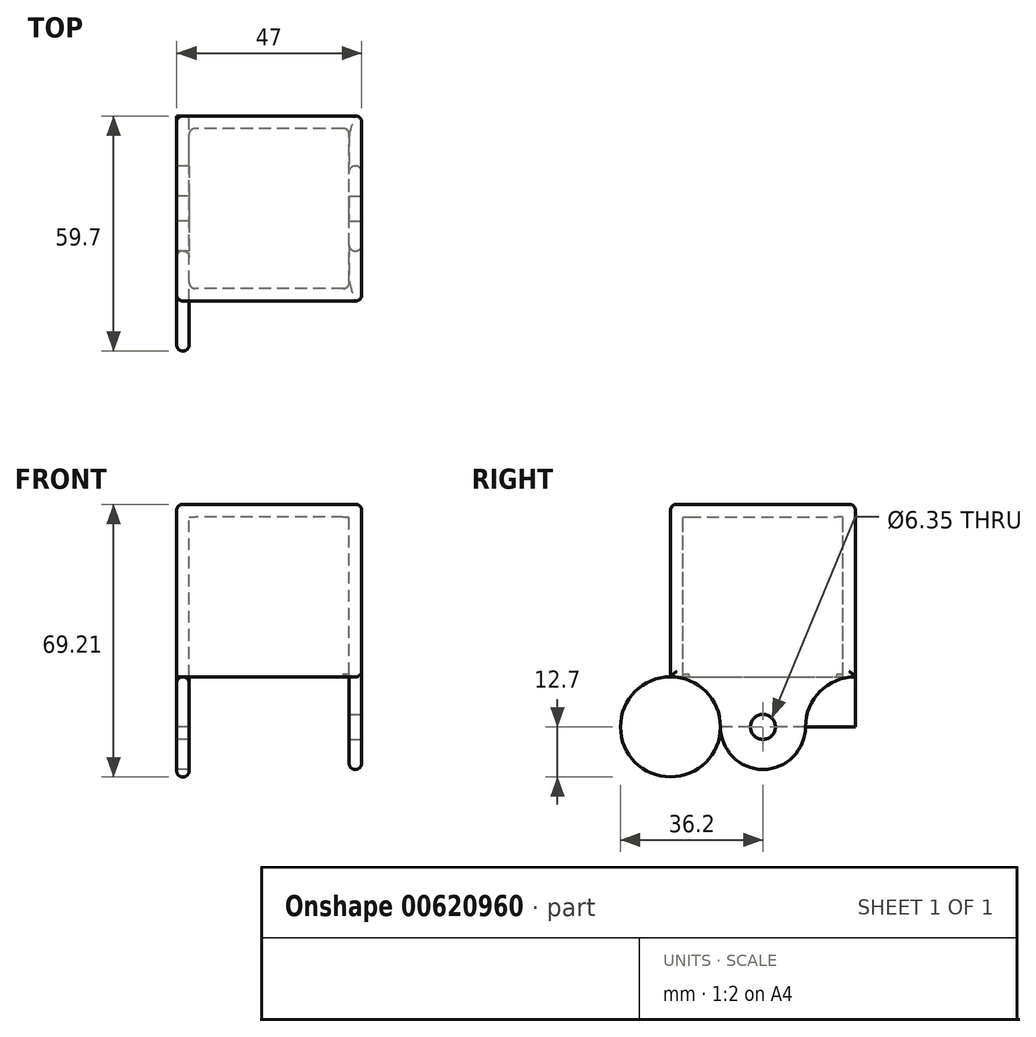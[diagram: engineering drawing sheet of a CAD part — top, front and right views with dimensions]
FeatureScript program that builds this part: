
annotation { "Feature Type Name" : "Feature", "Feature Type Description" : "" }
export const myFeature = defineFeature(function(context is Context, id is Id, definition is map)
    precondition{}
    {
        {
            var Q0;
            Q0=qCreatedBy(makeId("Top.planeOp"),FACE);
            var sketch = newSketch(context, id + "F0", { "sketchPlane" : qUnion([Q0])});
            skLineSegment(sketch, "E0.bottom", {"start": v(20.32, -20.32) * mm, "end": v(-20.32, -20.32) * mm});
            skLineSegment(sketch, "E0.top", {"start": v(20.32, 20.32) * mm, "end": v(-20.32, 20.32) * mm});
            skLineSegment(sketch, "E0.left", {"start": v(20.32, -20.32) * mm, "end": v(20.32, 20.32) * mm});
            skLineSegment(sketch, "E0.right", {"start": v(-20.32, -20.32) * mm, "end": v(-20.32, 20.32) * mm});
            skPoint(sketch, "E0.middle", {"position": v(0, 0) * mm});
            skLineSegment(sketch, "E1.0", {"start": v(-23.5, -20.32) * mm, "end": v(-23.5, 20.32) * mm});
            skLineSegment(sketch, "E1.1", {"start": v(20.32, -23.5) * mm, "end": v(-20.32, -23.5) * mm});
            skLineSegment(sketch, "E1.2", {"start": v(23.5, -20.32) * mm, "end": v(23.5, 20.32) * mm});
            skLineSegment(sketch, "E1.3", {"start": v(20.32, 23.5) * mm, "end": v(-20.32, 23.5) * mm});
            skPoint(sketch, "E2.visualSharp", {"position": v(-23.5, 23.5) * mm});
            skPoint(sketch, "E3.visualSharp", {"position": v(23.5, 23.5) * mm});
            skPoint(sketch, "E4.visualSharp", {"position": v(23.5, -23.5) * mm});
            skPoint(sketch, "E5.visualSharp", {"position": v(-23.5, -23.5) * mm});
            skLineSegment(sketch, "E6.bottom", {"start": v(20.32, 20.32) * mm, "end": v(23.5, 20.32) * mm});
            skLineSegment(sketch, "E6.top", {"start": v(20.32, 23.5) * mm, "end": v(23.5, 23.5) * mm});
            skLineSegment(sketch, "E6.left", {"start": v(20.32, 20.32) * mm, "end": v(20.32, 23.5) * mm});
            skLineSegment(sketch, "E6.right", {"start": v(23.5, 20.32) * mm, "end": v(23.5, 23.5) * mm});
            skLineSegment(sketch, "E7.bottom", {"start": v(20.32, -20.32) * mm, "end": v(23.5, -20.32) * mm});
            skLineSegment(sketch, "E7.top", {"start": v(20.32, -23.5) * mm, "end": v(23.5, -23.5) * mm});
            skLineSegment(sketch, "E7.left", {"start": v(20.32, -20.32) * mm, "end": v(20.32, -23.5) * mm});
            skLineSegment(sketch, "E7.right", {"start": v(23.5, -20.32) * mm, "end": v(23.5, -23.5) * mm});
            skLineSegment(sketch, "E8.bottom", {"start": v(-23.5, -23.5) * mm, "end": v(-20.32, -23.5) * mm});
            skLineSegment(sketch, "E8.top", {"start": v(-23.5, -20.32) * mm, "end": v(-20.32, -20.32) * mm});
            skLineSegment(sketch, "E8.left", {"start": v(-23.5, -23.5) * mm, "end": v(-23.5, -20.32) * mm});
            skLineSegment(sketch, "E8.right", {"start": v(-20.32, -23.5) * mm, "end": v(-20.32, -20.32) * mm});
            skLineSegment(sketch, "E9.bottom", {"start": v(-23.5, 23.5) * mm, "end": v(-20.32, 23.5) * mm});
            skLineSegment(sketch, "E9.top", {"start": v(-23.5, 20.32) * mm, "end": v(-20.32, 20.32) * mm});
            skLineSegment(sketch, "E9.left", {"start": v(-23.5, 23.5) * mm, "end": v(-23.5, 20.32) * mm});
            skLineSegment(sketch, "E9.right", {"start": v(-20.32, 23.5) * mm, "end": v(-20.32, 20.32) * mm});
            skSolve(sketch);
        }
        {
            var Q0;
            Q0=makeQuery(id+"F0.imprint","IMPRINT",FACE,{"disambiguationData":[TD([[makeQuery(id+"F0.imprint","IMPRINT",EDGE,{"derivedFrom":sQuery(id+"F0.wireOp",EDGE,"E0.bottom")}),-1.0]])]});
            var Q1;
            Q1=makeQuery(id+"F0.imprint","IMPRINT",FACE,{"disambiguationData":[TD([[makeQuery(id+"F0.imprint","IMPRINT",EDGE,{"derivedFrom":sQuery(id+"F0.wireOp",EDGE,"E0.bottom")}),1.0]])]});
            var Q2;
            Q2=makeQuery(id+"F0.imprint","IMPRINT",FACE,{"disambiguationData":[TD([[makeQuery(id+"F0.imprint","IMPRINT",EDGE,{"derivedFrom":sQuery(id+"F0.wireOp",EDGE,"E7.bottom")}),-1.0]])]});
            var Q3;
            Q3=makeQuery(id+"F0.imprint","IMPRINT",FACE,{"disambiguationData":[TD([[makeQuery(id+"F0.imprint","IMPRINT",EDGE,{"derivedFrom":sQuery(id+"F0.wireOp",EDGE,"E6.bottom")}),1.0]])]});
            var Q4;
            Q4=makeQuery(id+"F0.imprint","IMPRINT",FACE,{"disambiguationData":[TD([[makeQuery(id+"F0.imprint","IMPRINT",EDGE,{"derivedFrom":sQuery(id+"F0.wireOp",EDGE,"E0.top")}),-1.0]])]});
            var Q5;
            Q5=makeQuery(id+"F0.imprint","IMPRINT",FACE,{"disambiguationData":[TD([[makeQuery(id+"F0.imprint","IMPRINT",EDGE,{"derivedFrom":sQuery(id+"F0.wireOp",EDGE,"E9.bottom")}),-1.0]])]});
            var Q6;
            Q6=makeQuery(id+"F0.imprint","IMPRINT",FACE,{"disambiguationData":[TD([[makeQuery(id+"F0.imprint","IMPRINT",EDGE,{"derivedFrom":sQuery(id+"F0.wireOp",EDGE,"E0.right")}),1.0]])]});
            var Q7;
            Q7=makeQuery(id+"F0.imprint","IMPRINT",FACE,{"disambiguationData":[TD([[makeQuery(id+"F0.imprint","IMPRINT",EDGE,{"derivedFrom":sQuery(id+"F0.wireOp",EDGE,"E8.bottom")}),1.0]])]});
            var Q8;
            Q8=makeQuery(id+"F0.imprint","IMPRINT",FACE,{"disambiguationData":[TD([[makeQuery(id+"F0.imprint","IMPRINT",EDGE,{"derivedFrom":sQuery(id+"F0.wireOp",EDGE,"E0.left")}),-1.0]])]});
            extrude(context, id + "F1", {"entities" : qUnion([Q0, Q1, Q2, Q3, Q4, Q5, Q6, Q7, Q8]), "depth" : 3.17 * mm, "offsetDistance" : 25.4 * mm});
        }
        {
            var Q0;
            Q0=makeQuery(id+"F0.imprint","IMPRINT",FACE,{"disambiguationData":[TD([[makeQuery(id+"F0.imprint","IMPRINT",EDGE,{"derivedFrom":sQuery(id+"F0.wireOp",EDGE,"E0.bottom")}),1.0]])]});
            var Q1;
            Q1=makeQuery(id+"F0.imprint","IMPRINT",FACE,{"disambiguationData":[TD([[makeQuery(id+"F0.imprint","IMPRINT",EDGE,{"derivedFrom":sQuery(id+"F0.wireOp",EDGE,"E8.bottom")}),1.0]])]});
            var Q2;
            Q2=makeQuery(id+"F0.imprint","IMPRINT",FACE,{"disambiguationData":[TD([[makeQuery(id+"F0.imprint","IMPRINT",EDGE,{"derivedFrom":sQuery(id+"F0.wireOp",EDGE,"E0.right")}),1.0]])]});
            var Q3;
            Q3=makeQuery(id+"F0.imprint","IMPRINT",FACE,{"disambiguationData":[TD([[makeQuery(id+"F0.imprint","IMPRINT",EDGE,{"derivedFrom":sQuery(id+"F0.wireOp",EDGE,"E9.bottom")}),-1.0]])]});
            var Q4;
            Q4=makeQuery(id+"F0.imprint","IMPRINT",FACE,{"disambiguationData":[TD([[makeQuery(id+"F0.imprint","IMPRINT",EDGE,{"derivedFrom":sQuery(id+"F0.wireOp",EDGE,"E0.top")}),-1.0]])]});
            var Q5;
            Q5=makeQuery(id+"F0.imprint","IMPRINT",FACE,{"disambiguationData":[TD([[makeQuery(id+"F0.imprint","IMPRINT",EDGE,{"derivedFrom":sQuery(id+"F0.wireOp",EDGE,"E6.bottom")}),1.0]])]});
            var Q6;
            Q6=makeQuery(id+"F0.imprint","IMPRINT",FACE,{"disambiguationData":[TD([[makeQuery(id+"F0.imprint","IMPRINT",EDGE,{"derivedFrom":sQuery(id+"F0.wireOp",EDGE,"E0.left")}),-1.0]])]});
            var Q7;
            Q7=makeQuery(id+"F0.imprint","IMPRINT",FACE,{"disambiguationData":[TD([[makeQuery(id+"F0.imprint","IMPRINT",EDGE,{"derivedFrom":sQuery(id+"F0.wireOp",EDGE,"E7.bottom")}),-1.0]])]});
            extrude(context, id + "F2", {"entities" : qUnion([Q0, Q1, Q2, Q3, Q4, Q5, Q6, Q7]), "operationType" : NewBodyOperationType.ADD, "oppositeDirection" : true, "depth" : 40.64 * mm, "offsetDistance" : 25.4 * mm});
        }
        {
            var Q0;
            {var subQ0=sQuery(id+"F0.wireOp",EDGE,"E1.2");Q0=makeQuery(id+"F2.boolean.opBoolean","MERGE",FACE,{"derivedFrom":[makeQuery(id+"F1.opExtrude","SWEPT_FACE",FACE,{"disambiguationData":[OSD([subQ0])]}),makeQuery(id+"F2.opExtrude","SWEPT_FACE",FACE,{"disambiguationData":[OSD([subQ0])]})]});}
            var sketch = newSketch(context, id + "F3", { "sketchPlane" : qUnion([Q0])});
            skLineSegment(sketch, "E10", {"start": v(23.5, -40.64) * mm, "end": v(23.5, -53.34) * mm});
            skCircle(sketch, "E11", {"center": v(23.5, -53.34) * mm, "radius": 12.7 * mm});
            skLineSegment(sketch, "E12", {"start": v(23.5, -53.34) * mm, "end": v(-23.5, -53.34) * mm});
            skCircle(sketch, "E13", {"center": v(0, -53.34) * mm, "radius": 10.8 * mm});
            skCircle(sketch, "E14", {"center": v(-23.5, -53.34) * mm, "radius": 12.7 * mm});
            skCircle(sketch, "E15", {"center": v(0, -53.34) * mm, "radius": 3.18 * mm});
            skSolve(sketch);
        }
        {
            var Q0;
            {var subQ0=sQuery(id+"F3.wireOp",EDGE,"E11");var subQ5=sQuery(id+"F3.wireOp",EDGE,"E13");var subQ6=makeQuery(id+"F3.imprint","INTERSECT",VERTEX,{"derivedFrom":[subQ0,sQuery(id+"F3.wireOp",EDGE,"E12"),subQ5]});Q0=makeQuery(id+"F3.imprint","IMPRINT",FACE,{"disambiguationData":[TD([[makeQuery(id+"F3.imprint","IMPRINT",EDGE,{"disambiguationData":[TD([[subQ6,-1.0]])],"derivedFrom":subQ5}),-1.0]])]});}
            var Q1;
            {var subQ1=sQuery(id+"F3.wireOp",EDGE,"E12");var subQ5=sQuery(id+"F3.wireOp",EDGE,"E15");var subQ7=makeQuery(id+"F3.imprint","INTERSECT",VERTEX,{"disambiguationData":[OD(0.0)],"derivedFrom":[subQ1,subQ5]});Q1=makeQuery(id+"F3.imprint","IMPRINT",FACE,{"disambiguationData":[TD([[makeQuery(id+"F3.imprint","IMPRINT",EDGE,{"disambiguationData":[TD([[subQ7,-1.0]])],"derivedFrom":subQ5}),-1.0]])]});}
            var Q2;
            {var subQ0=sQuery(id+"F3.wireOp",EDGE,"E15");var subQ1=sQuery(id+"F3.wireOp",EDGE,"E12");var subQ2=makeQuery(id+"F3.imprint","INTERSECT",VERTEX,{"disambiguationData":[OD(0.0)],"derivedFrom":[subQ1,subQ0]});Q2=makeQuery(id+"F3.imprint","IMPRINT",FACE,{"disambiguationData":[TD([[makeQuery(id+"F3.imprint","IMPRINT",EDGE,{"disambiguationData":[TD([[subQ2,1.0]])],"derivedFrom":subQ0}),-1.0]])]});}
            var Q3;
            {var subQ0=sQuery(id+"F3.wireOp",EDGE,"E14");var subQ1=sQuery(id+"F3.wireOp",EDGE,"E13");var subQ2=makeQuery(id+"F3.imprint","INTERSECT",VERTEX,{"derivedFrom":[sQuery(id+"F3.wireOp",EDGE,"E12"),subQ1,subQ0]});Q3=makeQuery(id+"F3.imprint","IMPRINT",FACE,{"disambiguationData":[TD([[makeQuery(id+"F3.imprint","IMPRINT",EDGE,{"disambiguationData":[TD([[subQ2,1.0]])],"derivedFrom":subQ1}),-1.0]])]});}
            extrude(context, id + "F4", {"entities" : qUnion([Q0, Q1, Q2, Q3]), "operationType" : NewBodyOperationType.ADD, "oppositeDirection" : true, "depth" : 3.17 * mm, "offsetDistance" : 25.4 * mm});
        }
        {
            var Q0;
            {var subQ0=sQuery(id+"F0.wireOp",EDGE,"E9.left");var subQ1=sQuery(id+"F0.wireOp",EDGE,"E8.left");var subQ2=sQuery(id+"F0.wireOp",EDGE,"E1.0");Q0=makeQuery(id+"F2.boolean.opBoolean","MERGE",FACE,{"derivedFrom":[makeQuery(id+"F1.opExtrude","SWEPT_FACE",FACE,{"disambiguationData":[OSD([subQ2,subQ1,subQ0])]}),makeQuery(id+"F2.opExtrude","SWEPT_FACE",FACE,{"disambiguationData":[OSD([subQ2,subQ1,subQ0])]})]});}
            var sketch = newSketch(context, id + "F5", { "sketchPlane" : qUnion([Q0])});
            skArc(sketch, "E16.0.0", {"start": v(23.5, -40.64) * mm, "mid": v(32.48, -62.32) * mm, "end": v(10.8, -53.34) * mm});
            skArc(sketch, "E16.0.1", {"start": v(10.8, -53.34) * mm, "mid": v(14.51, -44.36) * mm, "end": v(23.5, -40.64) * mm});
            skLineSegment(sketch, "E17.0.0", {"start": v(-23.5, -53.34) * mm, "end": v(-23.5, -40.64) * mm});
            skArc(sketch, "E17.0.1", {"start": v(-23.5, -40.64) * mm, "mid": v(-14.51, -44.36) * mm, "end": v(-10.8, -53.34) * mm});
            skLineSegment(sketch, "E17.0.2", {"start": v(-10.8, -53.34) * mm, "end": v(-23.5, -53.34) * mm});
            skArc(sketch, "E18.0.0", {"start": v(-3.17, -53.34) * mm, "mid": v(0, -56.52) * mm, "end": v(3.18, -53.34) * mm});
            skLineSegment(sketch, "E18.0.1", {"start": v(3.18, -53.34) * mm, "end": v(10.8, -53.34) * mm});
            skArc(sketch, "E18.0.2", {"start": v(10.8, -53.34) * mm, "mid": v(0, -64.14) * mm, "end": v(-10.8, -53.34) * mm});
            skLineSegment(sketch, "E18.0.3", {"start": v(-10.8, -53.34) * mm, "end": v(-3.17, -53.34) * mm});
            skLineSegment(sketch, "E19.0.0", {"start": v(10.8, -53.34) * mm, "end": v(3.18, -53.34) * mm});
            skArc(sketch, "E19.0.1", {"start": v(3.18, -53.34) * mm, "mid": v(0, -50.17) * mm, "end": v(-3.17, -53.34) * mm});
            skLineSegment(sketch, "E19.0.2", {"start": v(-3.17, -53.34) * mm, "end": v(-10.8, -53.34) * mm});
            skArc(sketch, "E19.0.3", {"start": v(-10.8, -53.34) * mm, "mid": v(0, -42.55) * mm, "end": v(10.8, -53.34) * mm});
            skLineSegment(sketch, "E19.0.4", {"start": v(10.8, -53.34) * mm, "end": v(10.8, -53.34) * mm});
            skSolve(sketch);
        }
        {
            var Q0;
            {var subQ0=sQuery(id+"F5.wireOp",EDGE,"E16.0.1");Q0=makeQuery(id+"F5.imprint","IMPRINT",FACE,{"disambiguationData":[TD([[makeQuery(id+"F5.imprint","IMPRINT",EDGE,{"derivedFrom":subQ0}),1.0]])]});}
            var Q1;
            Q1=makeQuery(id+"F5.imprint","IMPRINT",FACE,{"disambiguationData":[TD([[makeQuery(id+"F5.imprint","IMPRINT",EDGE,{"derivedFrom":sQuery(id+"F5.wireOp",EDGE,"E19.0.0")}),-1.0]])]});
            var Q2;
            Q2=makeQuery(id+"F5.imprint","IMPRINT",FACE,{"disambiguationData":[TD([[makeQuery(id+"F5.imprint","IMPRINT",EDGE,{"derivedFrom":sQuery(id+"F5.wireOp",EDGE,"E18.0.0")}),-1.0]])]});
            var Q3;
            {var subQ0=sQuery(id+"F5.wireOp",EDGE,"E17.0.1");Q3=makeQuery(id+"F5.imprint","IMPRINT",FACE,{"disambiguationData":[TD([[makeQuery(id+"F5.imprint","IMPRINT",EDGE,{"derivedFrom":subQ0}),1.0]])]});}
            extrude(context, id + "F6", {"entities" : qUnion([Q0, Q1, Q2, Q3]), "operationType" : NewBodyOperationType.ADD, "oppositeDirection" : true, "depth" : 3.17 * mm, "offsetDistance" : 25.4 * mm});
        }
        {
            var Q0;
            {var subQ0=sQuery(id+"F0.wireOp",EDGE,"E6.right");var subQ1=sQuery(id+"F0.wireOp",EDGE,"E6.top");Q0=makeQuery(id+"F2.boolean.opBoolean","MERGE",EDGE,{"derivedFrom":[makeQuery(id+"F1.opExtrude","SWEPT_EDGE",EDGE,{"disambiguationData":[OSD([subQ1,subQ0])]}),makeQuery(id+"F2.opExtrude","SWEPT_EDGE",EDGE,{"disambiguationData":[OSD([subQ1,subQ0])]})]});}
            var Q1;
            {var subQ0=sQuery(id+"F0.wireOp",EDGE,"E9.left");var subQ1=sQuery(id+"F0.wireOp",EDGE,"E9.bottom");Q1=makeQuery(id+"F2.boolean.opBoolean","MERGE",EDGE,{"derivedFrom":[makeQuery(id+"F1.opExtrude","SWEPT_EDGE",EDGE,{"disambiguationData":[OSD([subQ1,subQ0])]}),makeQuery(id+"F2.opExtrude","SWEPT_EDGE",EDGE,{"disambiguationData":[OSD([subQ1,subQ0])]})]});}
            var Q2;
            Q2=makeQuery(id+"F1.opExtrude","CAP_EDGE",EDGE,{"disambiguationData":[OSD([sQuery(id+"F0.wireOp",EDGE,"E1.3"),sQuery(id+"F0.wireOp",EDGE,"E6.top"),sQuery(id+"F0.wireOp",EDGE,"E9.bottom")])],"isStart":false});
            var Q3;
            Q3=makeQuery(id+"F1.opExtrude","CAP_EDGE",EDGE,{"disambiguationData":[OSD([sQuery(id+"F0.wireOp",EDGE,"E1.2"),sQuery(id+"F0.wireOp",EDGE,"E6.right"),sQuery(id+"F0.wireOp",EDGE,"E7.right")])],"isStart":false});
            var Q4;
            Q4=makeQuery(id+"F1.opExtrude","CAP_EDGE",EDGE,{"disambiguationData":[OSD([sQuery(id+"F0.wireOp",EDGE,"E1.1"),sQuery(id+"F0.wireOp",EDGE,"E7.top"),sQuery(id+"F0.wireOp",EDGE,"E8.bottom")])],"isStart":false});
            var Q5;
            Q5=makeQuery(id+"F1.opExtrude","CAP_EDGE",EDGE,{"disambiguationData":[OSD([sQuery(id+"F0.wireOp",EDGE,"E1.0"),sQuery(id+"F0.wireOp",EDGE,"E8.left"),sQuery(id+"F0.wireOp",EDGE,"E9.left")])],"isStart":false});
            var Q6;
            {var subQ0=sQuery(id+"F0.wireOp",EDGE,"E7.right");var subQ1=sQuery(id+"F0.wireOp",EDGE,"E7.top");Q6=makeQuery(id+"F2.boolean.opBoolean","MERGE",EDGE,{"derivedFrom":[makeQuery(id+"F1.opExtrude","SWEPT_EDGE",EDGE,{"disambiguationData":[OSD([subQ1,subQ0])]}),makeQuery(id+"F2.opExtrude","SWEPT_EDGE",EDGE,{"disambiguationData":[OSD([subQ1,subQ0])]})]});}
            var Q7;
            {var subQ0=sQuery(id+"F0.wireOp",EDGE,"E8.left");var subQ1=sQuery(id+"F0.wireOp",EDGE,"E8.bottom");Q7=makeQuery(id+"F2.boolean.opBoolean","MERGE",EDGE,{"derivedFrom":[makeQuery(id+"F1.opExtrude","SWEPT_EDGE",EDGE,{"disambiguationData":[OSD([subQ1,subQ0])]}),makeQuery(id+"F2.opExtrude","SWEPT_EDGE",EDGE,{"disambiguationData":[OSD([subQ1,subQ0])]})]});}
            var Q8;
            Q8=makeQuery(id+"F6.opExtrude","CAP_EDGE",EDGE,{"disambiguationData":[OSD([sQuery(id+"F5.wireOp",EDGE,"E16.0.1")])],"isStart":true});
            var Q9;
            Q9=makeQuery(id+"F4.opExtrude","CAP_EDGE",EDGE,{"disambiguationData":[OSD([sQuery(id+"F3.wireOp",EDGE,"E14")])],"isStart":true});
            var Q10;
            Q10=makeQuery(id+"F4.opExtrude","CAP_EDGE",EDGE,{"disambiguationData":[OSD([sQuery(id+"F3.wireOp",EDGE,"E14")])],"isStart":false});
            var Q11;
            Q11=makeQuery(id+"F6.opExtrude","CAP_EDGE",EDGE,{"disambiguationData":[OSD([sQuery(id+"F5.wireOp",EDGE,"E16.0.1")])],"isStart":false});
            fillet(context, id + "F7", {"entities" : qUnion([Q0, Q1, Q2, Q3, Q4, Q5, Q6, Q7, Q8, Q9, Q10, Q11]), "radius" : 1.52 * mm, "tangentPropagation" : true, "allowEdgeOverflow" : false});
        }
        {
            var Q0;
            Q0=makeQuery(id+"F2.opExtrude","CAP_EDGE",EDGE,{"disambiguationData":[OSD([sQuery(id+"F0.wireOp",EDGE,"E0.top")])],"isStart":true});
            var Q1;
            Q1=makeQuery(id+"F2.opExtrude","CAP_EDGE",EDGE,{"disambiguationData":[OSD([sQuery(id+"F0.wireOp",EDGE,"E0.left")])],"isStart":true});
            var Q2;
            Q2=makeQuery(id+"F2.opExtrude","CAP_EDGE",EDGE,{"disambiguationData":[OSD([sQuery(id+"F0.wireOp",EDGE,"E0.right")])],"isStart":true});
            var Q3;
            Q3=makeQuery(id+"F2.opExtrude","CAP_EDGE",EDGE,{"disambiguationData":[OSD([sQuery(id+"F0.wireOp",EDGE,"E0.bottom")])],"isStart":true});
            var Q4;
            Q4=makeQuery(id+"F2.opExtrude","SWEPT_EDGE",EDGE,{"disambiguationData":[OSD([sQuery(id+"F0.wireOp",EDGE,"E0.bottom"),sQuery(id+"F0.wireOp",EDGE,"E0.right"),sQuery(id+"F0.wireOp",EDGE,"E8.top"),sQuery(id+"F0.wireOp",EDGE,"E8.right")])]});
            var Q5;
            Q5=makeQuery(id+"F2.opExtrude","SWEPT_EDGE",EDGE,{"disambiguationData":[OSD([sQuery(id+"F0.wireOp",EDGE,"E0.top"),sQuery(id+"F0.wireOp",EDGE,"E0.right"),sQuery(id+"F0.wireOp",EDGE,"E9.top"),sQuery(id+"F0.wireOp",EDGE,"E9.right")])]});
            var Q6;
            Q6=makeQuery(id+"F2.opExtrude","SWEPT_EDGE",EDGE,{"disambiguationData":[OSD([sQuery(id+"F0.wireOp",EDGE,"E0.top"),sQuery(id+"F0.wireOp",EDGE,"E0.left"),sQuery(id+"F0.wireOp",EDGE,"E6.bottom"),sQuery(id+"F0.wireOp",EDGE,"E6.left")])]});
            var Q7;
            Q7=makeQuery(id+"F2.opExtrude","SWEPT_EDGE",EDGE,{"disambiguationData":[OSD([sQuery(id+"F0.wireOp",EDGE,"E0.bottom"),sQuery(id+"F0.wireOp",EDGE,"E0.left"),sQuery(id+"F0.wireOp",EDGE,"E7.bottom"),sQuery(id+"F0.wireOp",EDGE,"E7.left")])]});
            fillet(context, id + "F8", {"entities" : qUnion([Q0, Q1, Q2, Q3, Q4, Q5, Q6, Q7]), "radius" : 1.52 * mm, "tangentPropagation" : true, "allowEdgeOverflow" : false});
        }
    });
